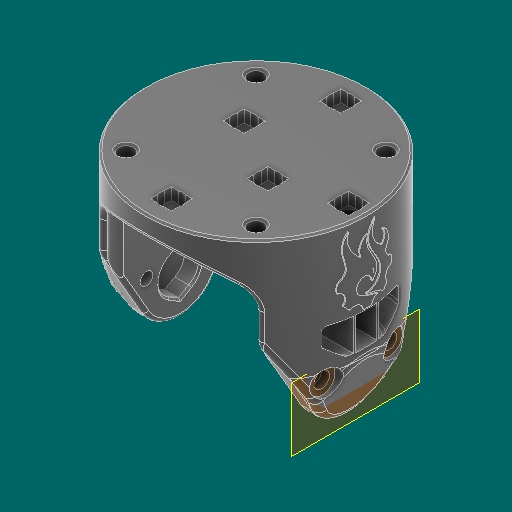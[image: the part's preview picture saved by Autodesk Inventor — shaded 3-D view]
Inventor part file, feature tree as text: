
AUTODESK INVENTOR PART (.ipt)
format: ipt  version: 2023.1 (Build 271208000, 208)  size: 1,963,008 bytes
history: native  units: in
note: dims shown in document units (in); Inventor stores cm internally (conversion verified against a paired STEP export)
features: sketch x14, other x13, plane x5
ambient origin geometry x8: Origin, YZ Plane, XZ Plane, XY Plane, X Axis, Y Axis, Z Axis, Center Point
bodies: Solid5 (feature_tree), Solid6 (feature_tree), Solid1 (feature_tree), Solid3 (feature_tree)
feature tree (32):
  other  "Carriage.ipt"
  other  "Solid1::Carriage.ipt"
  other  "Solid2::Carriage.ipt"
  other  "Solid3::Carriage.ipt"
  other  "Solid4::Carriage.ipt"
  other  "Solid5::Carriage.ipt"
  other  "TaggingFeature1"
  sketch  "Sketch2"  dims[d0=0.3937in]
  sketch  "Sketch3"
  sketch  "Sketch5"
  sketch  "Sketch11"
  sketch  "Sketch6"
  sketch  "Sketch7"
  sketch  "Sketch8"
  sketch  "Sketch9"
  sketch  "Sketch13"
  sketch  "Sketch14"
  sketch  "Sketch16"
  sketch  "Sketch17"
  sketch  "Sketch18"
  sketch  "Sketch19"
  plane  "Work Plane1"
  plane  "Work Plane3"
  plane  "Work Plane4"
  plane  "Work Plane5"
  plane  "Work Plane6"
  other  "Work Axis1"
  other  "Work Axis2"
  other  "Srf1"
  other  "Srf2"
  other  "Srf1::Derived"
  other  "Srf2::Derived"
